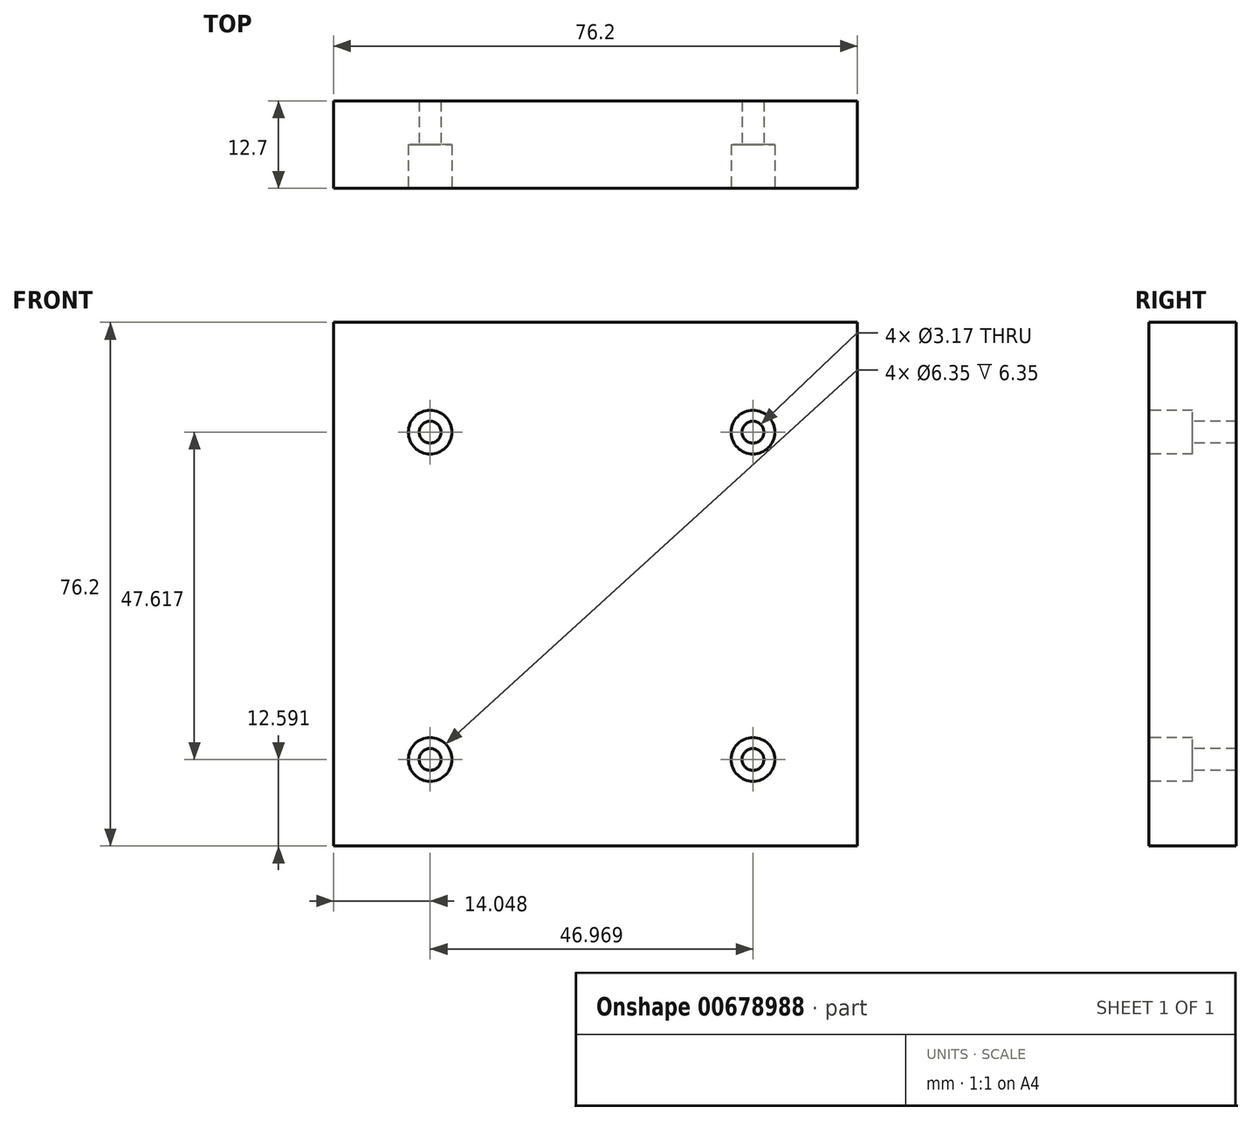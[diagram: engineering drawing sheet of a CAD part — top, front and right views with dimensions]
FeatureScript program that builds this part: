
annotation { "Feature Type Name" : "Feature", "Feature Type Description" : "" }
export const myFeature = defineFeature(function(context is Context, id is Id, definition is map)
    precondition{}
    {
        {
            var Q0;
            Q0=qCreatedBy(makeId("Front.planeOp"),FACE);
            var sketch = newSketch(context, id + "F0", { "sketchPlane" : qUnion([Q0])});
            skLineSegment(sketch, "E0.bottom", {"start": v(38.1, 38.1) * mm, "end": v(-38.1, 38.1) * mm});
            skLineSegment(sketch, "E0.top", {"start": v(38.1, -38.1) * mm, "end": v(-38.1, -38.1) * mm});
            skLineSegment(sketch, "E0.left", {"start": v(38.1, 38.1) * mm, "end": v(38.1, -38.1) * mm});
            skLineSegment(sketch, "E0.right", {"start": v(-38.1, 38.1) * mm, "end": v(-38.1, -38.1) * mm});
            skPoint(sketch, "E0.middle", {"position": v(0, 0) * mm});
            skSolve(sketch);
        }
        {
            var Q0;
            Q0 = qSketchRegion(id + "F0", true);
            extrude(context, id + "F1", {"entities" : qUnion([Q0]), "depth" : 12.7 * mm, "offsetDistance" : 25.4 * mm});
        }
        {
            var Q0;
            Q0=makeQuery(id+"F1.opExtrude","CAP_FACE",FACE,{"disambiguationData":[OSD([sQuery(id+"F0.wireOp",EDGE,"E0.bottom"),sQuery(id+"F0.wireOp",EDGE,"E0.top"),sQuery(id+"F0.wireOp",EDGE,"E0.left"),sQuery(id+"F0.wireOp",EDGE,"E0.right")])],"isStart":false});
            var sketch = newSketch(context, id + "F2", { "sketchPlane" : qUnion([Q0])});
            skPoint(sketch, "E1", {"position": v(-24.05, 22.1) * mm});
            skPoint(sketch, "E2", {"position": v(22.92, 22.1) * mm});
            skPoint(sketch, "E3", {"position": v(22.92, -25.5) * mm});
            skPoint(sketch, "E4", {"position": v(-24.05, -25.5) * mm});
            skSolve(sketch);
        }
        {
            var Q0;
            Q0=sQuery(id+"F2.wireOp",VERTEX,"E1");
            var Q1;
            Q1=sQuery(id+"F2.wireOp",VERTEX,"E2");
            var Q2;
            Q2=sQuery(id+"F2.wireOp",VERTEX,"E3");
            var Q3;
            Q3=sQuery(id+"F2.wireOp",VERTEX,"E4");
            var Q4;
            Q4=makeQuery(id+"F1.opExtrude","SWEPT_BODY",BODY,{"disambiguationData":[OSD([sQuery(id+"F0.wireOp",EDGE,"E0.bottom"),sQuery(id+"F0.wireOp",EDGE,"E0.top"),sQuery(id+"F0.wireOp",EDGE,"E0.left"),sQuery(id+"F0.wireOp",EDGE,"E0.right")])]});
            hole(context, id + "F3", {"style" : HoleStyle.C_BORE, "endStyle" : HoleEndStyle.THROUGH, "holeDiameter" : 3.17 * mm, "cBoreDiameter" : 6.35 * mm, "cBoreDepth" : 6.35 * mm, "majorDiameter" : 6.35 * mm, "isTappedThrough" : true, "tappedDepth" : 12.7 * mm, "tapClearance" : 3, "locations" : qUnion([Q0, Q1, Q2, Q3]), "scope" : qUnion([Q4])});
        }
    });
